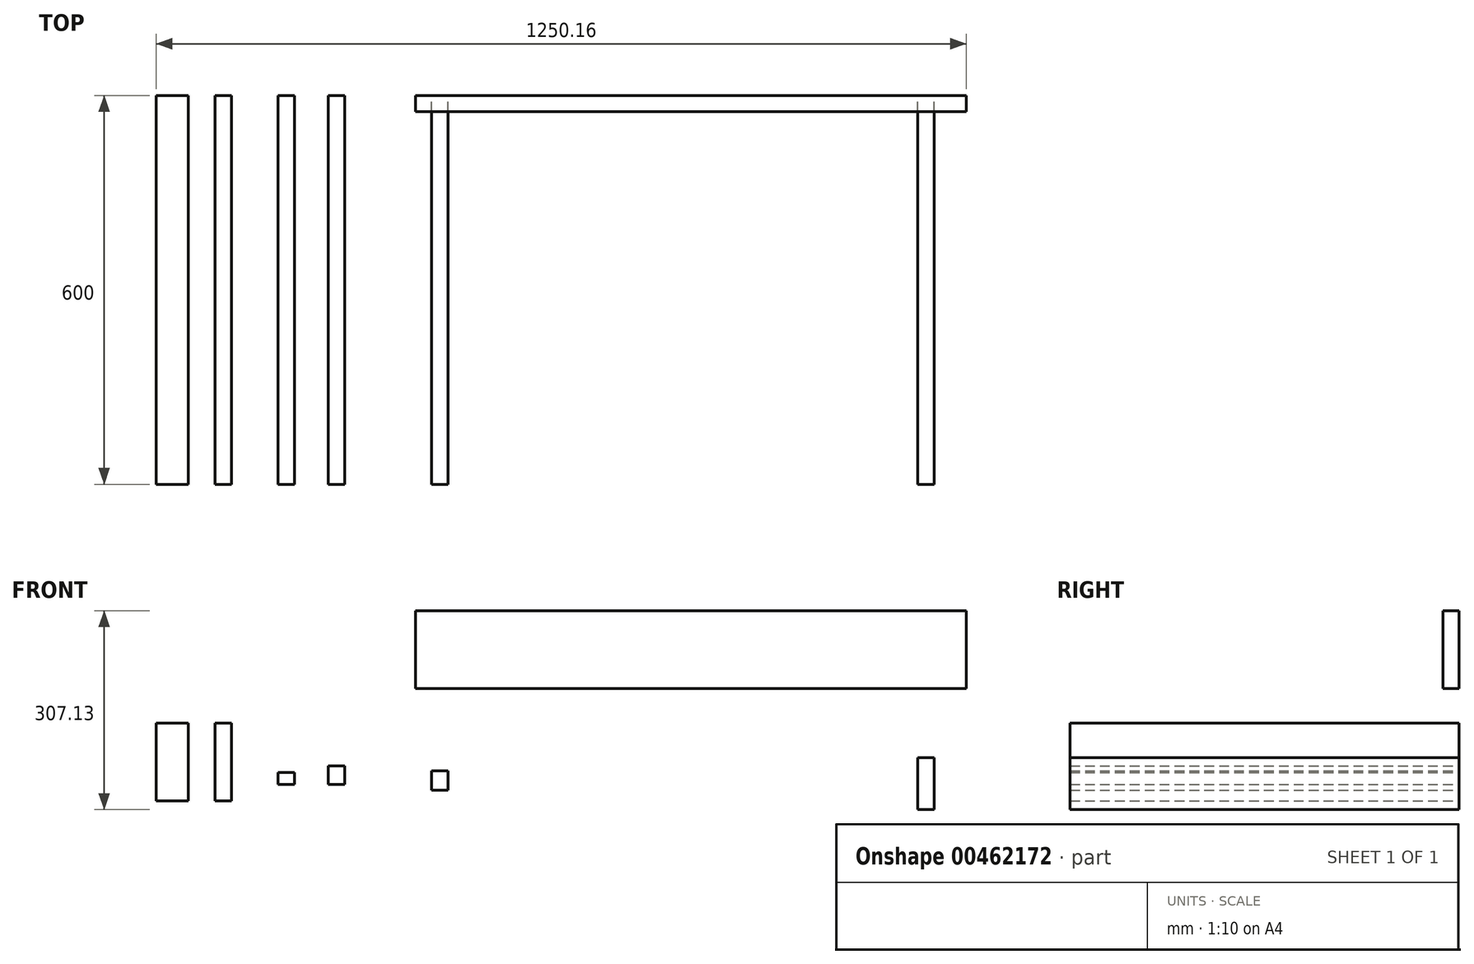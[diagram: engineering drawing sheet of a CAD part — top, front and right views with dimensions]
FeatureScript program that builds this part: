
annotation { "Feature Type Name" : "Feature", "Feature Type Description" : "" }
export const myFeature = defineFeature(function(context is Context, id is Id, definition is map)
    precondition{}
    {
        {
            var Q0;
            Q0=qCreatedBy(makeId("Front.planeOp"),FACE);
            var sketch = newSketch(context, id + "F0", { "sketchPlane" : qUnion([Q0])});
            skLineSegment(sketch, "E0.bottom", {"start": v(425, -60) * mm, "end": v(-425, -60) * mm});
            skLineSegment(sketch, "E0.top", {"start": v(425, 60) * mm, "end": v(-425, 60) * mm});
            skLineSegment(sketch, "E0.left", {"start": v(425, -60) * mm, "end": v(425, 60) * mm});
            skLineSegment(sketch, "E0.right", {"start": v(-425, -60) * mm, "end": v(-425, 60) * mm});
            skPoint(sketch, "E0.middle", {"position": v(0, 0) * mm});
            skSolve(sketch);
        }
        {
            var Q0;
            Q0 = qSketchRegion(id + "F0", true);
            extrude(context, id + "F1", {"entities" : qUnion([Q0]), "depth" : 25 * mm});
        }
        {
            var Q0;
            Q0=qCreatedBy(makeId("Front.planeOp"),FACE);
            var sketch = newSketch(context, id + "F2", { "sketchPlane" : qUnion([Q0])});
            skLineSegment(sketch, "E1.bottom", {"start": v(425, -272.13) * mm, "end": v(-425, -272.13) * mm, "construction": true});
            skLineSegment(sketch, "E1.top", {"start": v(425, -152.13) * mm, "end": v(-425, -152.13) * mm, "construction": true});
            skLineSegment(sketch, "E1.left", {"start": v(425, -272.13) * mm, "end": v(425, -152.13) * mm, "construction": true});
            skLineSegment(sketch, "E1.right", {"start": v(-425, -272.13) * mm, "end": v(-425, -152.13) * mm, "construction": true});
            skPoint(sketch, "E1.middle", {"position": v(0, -212.13) * mm});
            skLineSegment(sketch, "E2", {"start": v(0, -152.13) * mm, "end": v(0, -272.13) * mm, "construction": true});
            skPoint(sketch, "E3", {"position": v(-400, -152.13) * mm});
            skPoint(sketch, "E4", {"position": v(-375, -152.13) * mm});
            skLineSegment(sketch, "E5", {"start": v(-400, -152.13) * mm, "end": v(-400, -187.13) * mm, "construction": true});
            skLineSegment(sketch, "E6", {"start": v(-375, -152.13) * mm, "end": v(-375, -187.13) * mm, "construction": true});
            skPoint(sketch, "E7", {"position": v(-350, -152.13) * mm});
            skLineSegment(sketch, "E8", {"start": v(-350, -152.13) * mm, "end": v(-350, -272.13) * mm, "construction": true});
            skPoint(sketch, "E9", {"position": v(-425, -247.13) * mm});
            skLineSegment(sketch, "E10", {"start": v(-425, -247.13) * mm, "end": v(425, -247.13) * mm, "construction": true});
            skLineSegment(sketch, "E11", {"start": v(-425, -167.13) * mm, "end": v(425, -167.13) * mm, "construction": true});
            skPoint(sketch, "E12", {"position": v(-425, -187.13) * mm});
            skLineSegment(sketch, "E13", {"start": v(-400, -187.13) * mm, "end": v(-375, -187.13) * mm});
            skLineSegment(sketch, "E14.trimOffspring", {"start": v(-400, -247.13) * mm, "end": v(-400, -272.13) * mm, "construction": true});
            skPoint(sketch, "E15.orphan", {"position": v(-400, -212.13) * mm});
            skLineSegment(sketch, "E16.trimOffspring", {"start": v(-375, -247.13) * mm, "end": v(-375, -272.13) * mm, "construction": true});
            skPoint(sketch, "E17.orphan", {"position": v(-375, -212.13) * mm});
            skLineSegment(sketch, "E18", {"start": v(-375, -187.13) * mm, "end": v(-375, -217.13) * mm});
            skLineSegment(sketch, "E19", {"start": v(-375, -217.13) * mm, "end": v(-400, -217.13) * mm});
            skLineSegment(sketch, "E20", {"start": v(-400, -217.13) * mm, "end": v(-400, -187.13) * mm});
            skLineSegment(sketch, "E21.MirrorCS", {"start": v(350, -152.13) * mm, "end": v(350, -272.13) * mm, "construction": true});
            skLineSegment(sketch, "E22.MirrorCS", {"start": v(375, -152.13) * mm, "end": v(375, -187.13) * mm, "construction": true});
            skLineSegment(sketch, "E23.bottom", {"start": v(350, -167.13) * mm, "end": v(375, -167.13) * mm});
            skLineSegment(sketch, "E23.top", {"start": v(350, -247.13) * mm, "end": v(375, -247.13) * mm});
            skLineSegment(sketch, "E23.left", {"start": v(350, -167.13) * mm, "end": v(350, -247.13) * mm});
            skLineSegment(sketch, "E23.right", {"start": v(375, -167.13) * mm, "end": v(375, -247.13) * mm});
            skPoint(sketch, "E24", {"position": v(-425, -212.13) * mm});
            skSolve(sketch);
        }
        {
            var Q0;
            Q0 = qSketchRegion(id + "F2", true);
            extrude(context, id + "F3", {"entities" : qUnion([Q0]), "depth" : 600 * mm});
        }
        {
            var Q0;
            Q0=qCreatedBy(makeId("Front.planeOp"),FACE);
            var sketch = newSketch(context, id + "F4", { "sketchPlane" : qUnion([Q0])});
            skLineSegment(sketch, "E25.bottom", {"start": v(-708.93, -233.45) * mm, "end": v(-733.93, -233.45) * mm});
            skLineSegment(sketch, "E25.top", {"start": v(-708.93, -113.45) * mm, "end": v(-733.93, -113.45) * mm});
            skLineSegment(sketch, "E25.left", {"start": v(-708.93, -233.45) * mm, "end": v(-708.93, -113.45) * mm});
            skLineSegment(sketch, "E25.right", {"start": v(-733.93, -233.45) * mm, "end": v(-733.93, -113.45) * mm});
            skPoint(sketch, "E25.middle", {"position": v(-721.43, -173.45) * mm});
            skLineSegment(sketch, "E26.bottom", {"start": v(-611.85, -208.48) * mm, "end": v(-636.85, -208.48) * mm});
            skLineSegment(sketch, "E26.top", {"start": v(-611.85, -189.48) * mm, "end": v(-636.85, -189.48) * mm});
            skLineSegment(sketch, "E26.left", {"start": v(-611.85, -208.48) * mm, "end": v(-611.85, -189.48) * mm});
            skLineSegment(sketch, "E26.right", {"start": v(-636.85, -208.48) * mm, "end": v(-636.85, -189.48) * mm});
            skPoint(sketch, "E26.middle", {"position": v(-624.35, -198.98) * mm});
            skLineSegment(sketch, "E27.bottom", {"start": v(-534.25, -208.48) * mm, "end": v(-559.25, -208.48) * mm});
            skLineSegment(sketch, "E27.top", {"start": v(-534.25, -179.48) * mm, "end": v(-559.25, -179.48) * mm});
            skLineSegment(sketch, "E27.left", {"start": v(-534.25, -208.48) * mm, "end": v(-534.25, -179.48) * mm});
            skLineSegment(sketch, "E27.right", {"start": v(-559.25, -208.48) * mm, "end": v(-559.25, -179.48) * mm});
            skPoint(sketch, "E27.middle", {"position": v(-546.75, -193.98) * mm});
            skLineSegment(sketch, "E28.bottom", {"start": v(-775.16, -233.45) * mm, "end": v(-825.16, -233.45) * mm});
            skLineSegment(sketch, "E28.top", {"start": v(-775.16, -113.45) * mm, "end": v(-825.16, -113.45) * mm});
            skLineSegment(sketch, "E28.left", {"start": v(-775.16, -233.45) * mm, "end": v(-775.16, -113.45) * mm});
            skLineSegment(sketch, "E28.right", {"start": v(-825.16, -233.45) * mm, "end": v(-825.16, -113.45) * mm});
            skPoint(sketch, "E28.middle", {"position": v(-800.16, -173.45) * mm});
            skSolve(sketch);
        }
        {
            var Q0;
            Q0 = qSketchRegion(id + "F4", true);
            extrude(context, id + "F5", {"entities" : qUnion([Q0]), "depth" : 600 * mm});
        }
    });
